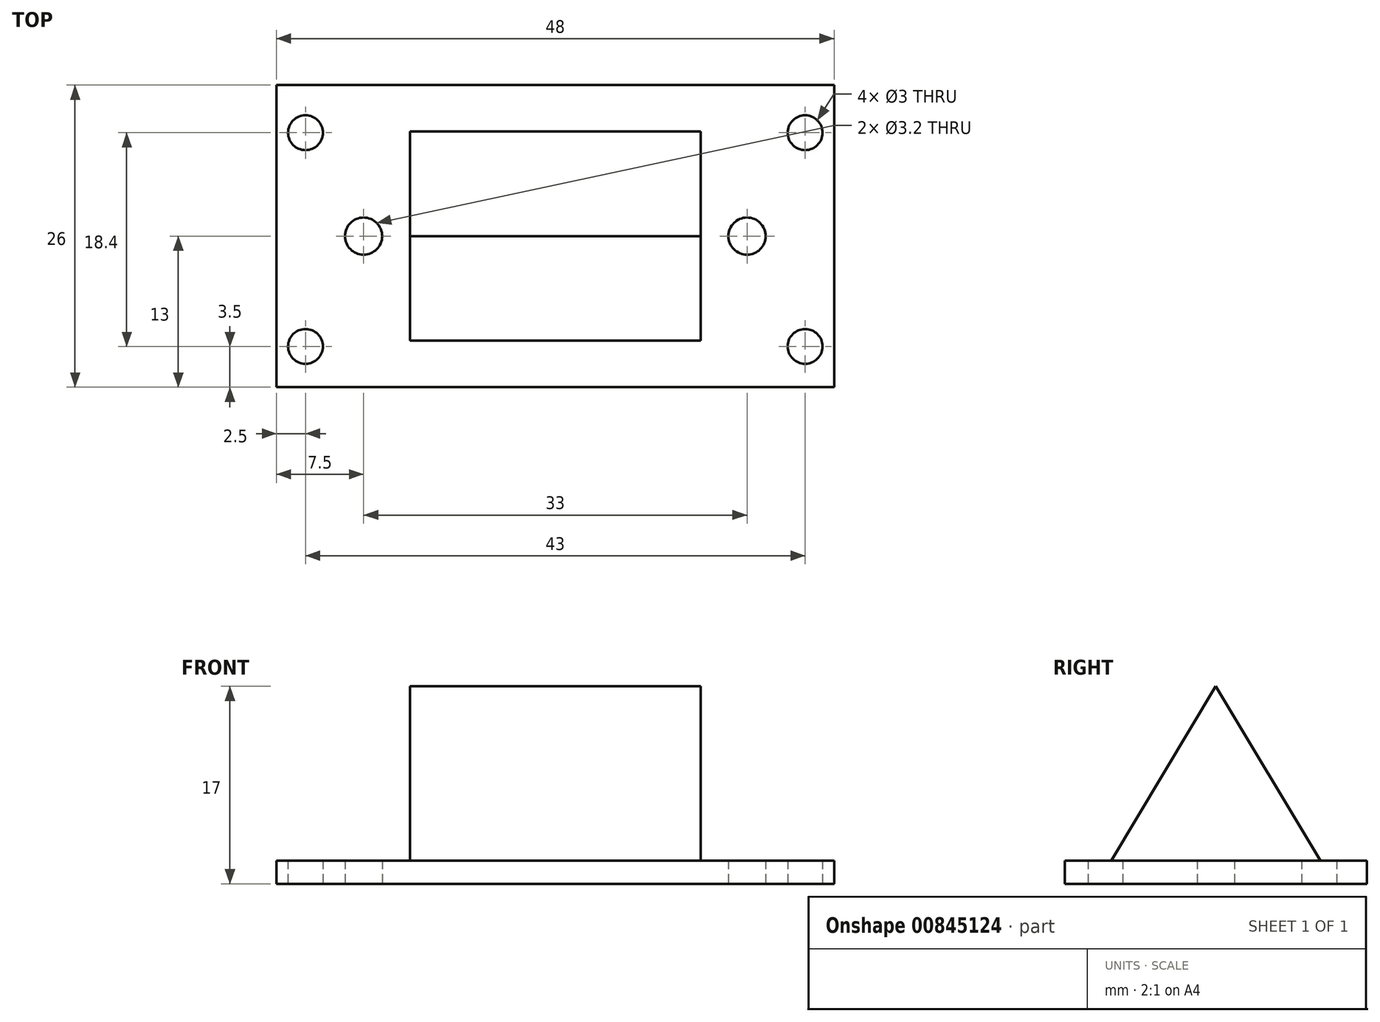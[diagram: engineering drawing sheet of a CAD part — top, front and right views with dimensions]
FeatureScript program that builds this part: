
annotation { "Feature Type Name" : "Feature", "Feature Type Description" : "" }
export const myFeature = defineFeature(function(context is Context, id is Id, definition is map)
    precondition{}
    {
        {
            var Q0;
            Q0=qCreatedBy(makeId("Top.planeOp"),FACE);
            var sketch = newSketch(context, id + "F0", { "sketchPlane" : qUnion([Q0])});
            skLineSegment(sketch, "E0.bottom", {"start": v(24, -13) * mm, "end": v(-24, -13) * mm});
            skLineSegment(sketch, "E0.top", {"start": v(24, 13) * mm, "end": v(-24, 13) * mm});
            skLineSegment(sketch, "E0.left", {"start": v(24, -13) * mm, "end": v(24, 13) * mm});
            skLineSegment(sketch, "E0.right", {"start": v(-24, -13) * mm, "end": v(-24, 13) * mm});
            skPoint(sketch, "E0.middle", {"position": v(0, 0) * mm});
            skLineSegment(sketch, "E1.bottom", {"start": v(21.5, -9.5) * mm, "end": v(-21.5, -9.5) * mm, "construction": true});
            skLineSegment(sketch, "E1.top", {"start": v(21.5, 8.9) * mm, "end": v(-21.5, 8.9) * mm, "construction": true});
            skLineSegment(sketch, "E1.left", {"start": v(21.5, -9.5) * mm, "end": v(21.5, 8.9) * mm, "construction": true});
            skLineSegment(sketch, "E1.right", {"start": v(-21.5, -9.5) * mm, "end": v(-21.5, 8.9) * mm, "construction": true});
            skCircle(sketch, "E2", {"center": v(-21.5, 8.9) * mm, "radius": 1.5 * mm});
            skCircle(sketch, "E3", {"center": v(-21.5, -9.5) * mm, "radius": 1.5 * mm});
            skCircle(sketch, "E4", {"center": v(21.5, -9.5) * mm, "radius": 1.5 * mm});
            skCircle(sketch, "E5", {"center": v(21.5, 8.9) * mm, "radius": 1.5 * mm});
            skLineSegment(sketch, "E6", {"start": v(24, 0) * mm, "end": v(-24, 0) * mm, "construction": true});
            skCircle(sketch, "E7", {"center": v(-16.5, 0) * mm, "radius": 1.6 * mm});
            skCircle(sketch, "E8", {"center": v(16.5, 0) * mm, "radius": 1.6 * mm});
            skSolve(sketch);
        }
        {
            var Q0;
            Q0 = qSketchRegion(id + "F0", true);
            extrude(context, id + "F1", {"entities" : qUnion([Q0]), "depth" : 2 * mm, "offsetDistance" : 25 * mm});
        }
        {
            var Q0;
            Q0=makeQuery(id+"F1.opExtrude","CAP_FACE",FACE,{"disambiguationData":[OSD([sQuery(id+"F0.wireOp",EDGE,"E0.bottom"),sQuery(id+"F0.wireOp",EDGE,"E0.top"),sQuery(id+"F0.wireOp",EDGE,"E0.left"),sQuery(id+"F0.wireOp",EDGE,"E0.right"),sQuery(id+"F0.wireOp",EDGE,"E2"),sQuery(id+"F0.wireOp",EDGE,"E3"),sQuery(id+"F0.wireOp",EDGE,"E4"),sQuery(id+"F0.wireOp",EDGE,"E5")])],"isStart":false});
            var sketch = newSketch(context, id + "F2", { "sketchPlane" : qUnion([Q0])});
            skLineSegment(sketch, "E9.bottom", {"start": v(12.5, -9) * mm, "end": v(-12.5, -9) * mm});
            skLineSegment(sketch, "E9.top", {"start": v(12.5, 9) * mm, "end": v(-12.5, 9) * mm});
            skLineSegment(sketch, "E9.left", {"start": v(12.5, -9) * mm, "end": v(12.5, 9) * mm});
            skLineSegment(sketch, "E9.right", {"start": v(-12.5, -9) * mm, "end": v(-12.5, 9) * mm});
            skPoint(sketch, "E9.middle", {"position": v(0, 0) * mm});
            skSolve(sketch);
        }
        {
            var Q0;
            Q0 = qSketchRegion(id + "F2", true);
            extrude(context, id + "F3", {"entities" : qUnion([Q0]), "operationType" : NewBodyOperationType.ADD, "depth" : 15 * mm, "offsetDistance" : 25 * mm});
        }
        {
            var Q0;
            Q0=makeQuery(id+"F3.opExtrude","SWEPT_FACE",FACE,{"disambiguationData":[OSD([sQuery(id+"F2.wireOp",EDGE,"E9.right")])]});
            var sketch = newSketch(context, id + "F4", { "sketchPlane" : qUnion([Q0])});
            skLineSegment(sketch, "E10", {"start": v(-9, 2) * mm, "end": v(0, 17) * mm});
            skLineSegment(sketch, "E11", {"start": v(0, 17) * mm, "end": v(9, 2) * mm});
            skLineSegment(sketch, "E12", {"start": v(9, 2) * mm, "end": v(9, 17) * mm});
            skLineSegment(sketch, "E13", {"start": v(9, 17) * mm, "end": v(-9, 17) * mm});
            skLineSegment(sketch, "E14", {"start": v(-9, 17) * mm, "end": v(-9, 2) * mm});
            skSolve(sketch);
        }
        {
            var Q0;
            Q0 = qSketchRegion(id + "F4", true);
            extrude(context, id + "F5", {"entities" : qUnion([Q0]), "operationType" : NewBodyOperationType.REMOVE, "oppositeDirection" : true, "depth" : 25 * mm, "offsetDistance" : 25 * mm});
        }
    });
